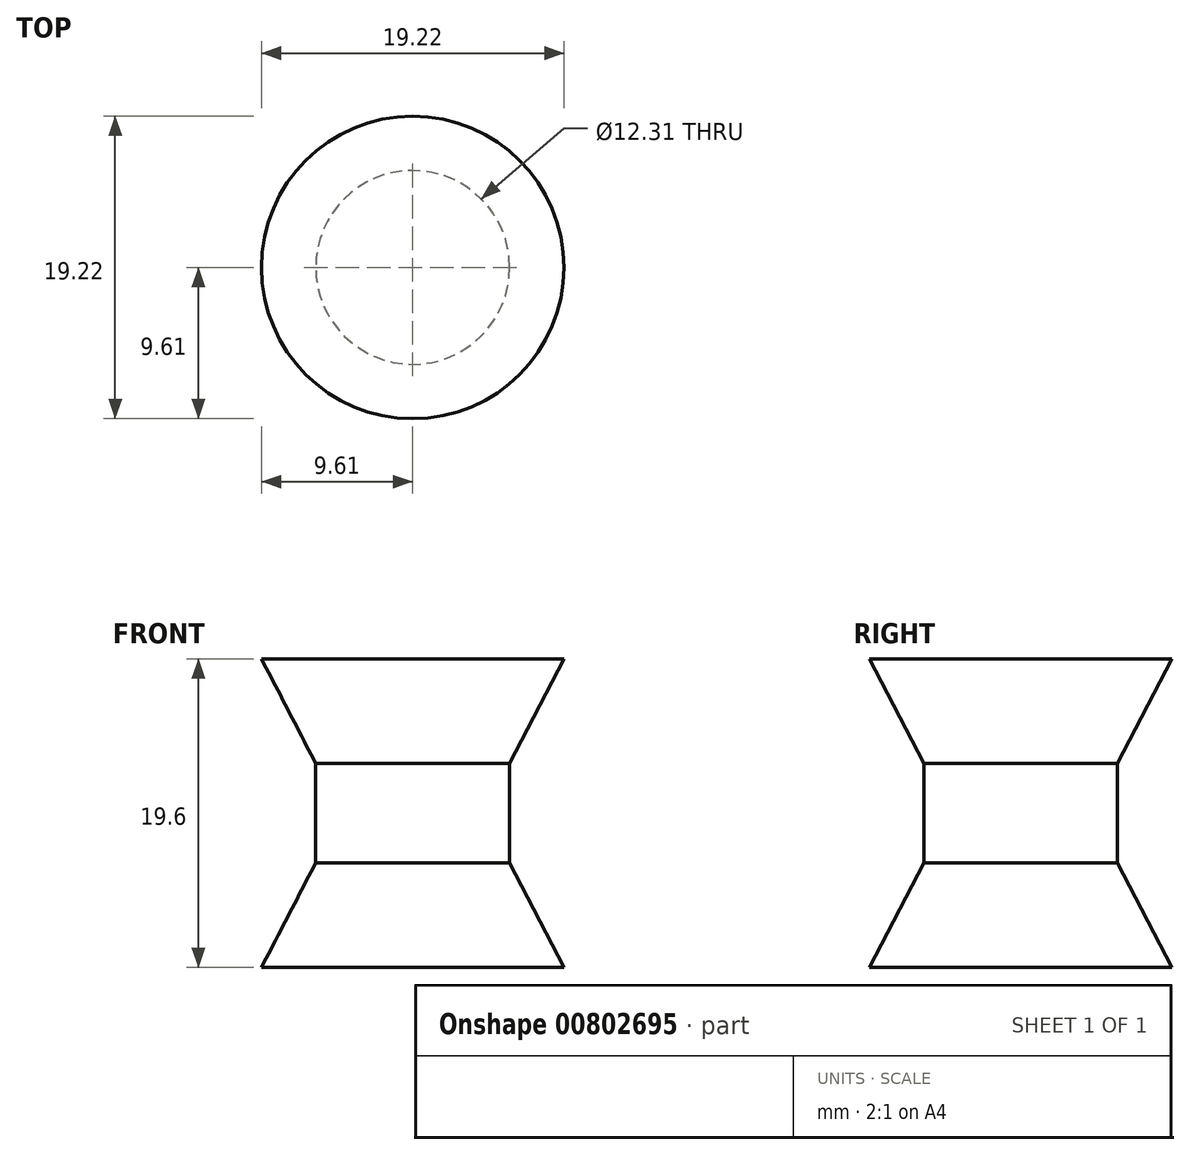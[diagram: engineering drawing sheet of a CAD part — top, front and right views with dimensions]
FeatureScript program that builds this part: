
annotation { "Feature Type Name" : "Feature", "Feature Type Description" : "" }
export const myFeature = defineFeature(function(context is Context, id is Id, definition is map)
    precondition{}
    {
        {
            var Q0;
            Q0=qCreatedBy(makeId("Front.planeOp"),FACE);
            var sketch = newSketch(context, id + "F0", { "sketchPlane" : qUnion([Q0])});
            skLineSegment(sketch, "E0", {"start": v(9.6, 9.8) * mm, "end": v(6.16, 3.15) * mm});
            skLineSegment(sketch, "E1", {"start": v(6.16, 3.15) * mm, "end": v(6.16, 0) * mm});
            skLineSegment(sketch, "E2", {"start": v(0, 0) * mm, "end": v(4.48, 0) * mm, "construction": true});
            skLineSegment(sketch, "E3.MirrorCS", {"start": v(9.6, -9.8) * mm, "end": v(6.16, -3.15) * mm});
            skLineSegment(sketch, "E4.MirrorCS", {"start": v(6.16, -3.15) * mm, "end": v(6.16, 0) * mm});
            skLineSegment(sketch, "E5", {"start": v(9.6, 9.8) * mm, "end": v(0, 9.8) * mm});
            skLineSegment(sketch, "E6", {"start": v(0, 9.8) * mm, "end": v(0, 0) * mm, "construction": true});
            skLineSegment(sketch, "E7.MirrorCS", {"start": v(9.6, -9.8) * mm, "end": v(0, -9.8) * mm});
            skSolve(sketch);
        }
        {
            var Q0;
            Q0=sQuery(id+"F0.wireOp",EDGE,"E0");
            var Q1;
            Q1=sQuery(id+"F0.wireOp",EDGE,"E1");
            var Q2;
            Q2=sQuery(id+"F0.wireOp",EDGE,"E4.MirrorCS");
            var Q3;
            Q3=sQuery(id+"F0.wireOp",EDGE,"E3.MirrorCS");
            var Q4;
            Q4=sQuery(id+"F0.wireOp",EDGE,"E5");
            var Q5;
            Q5=sQuery(id+"F0.wireOp",EDGE,"E6");
            revolve(context, id + "F1", {"bodyType" : ToolBodyType.SURFACE, "surfaceOperationType" : NewSurfaceOperationType.NEW, "surfaceEntities" : qUnion([Q0, Q1, Q2, Q3, Q4]), "axis" : qUnion([Q5]), "revolveType" : RevolveType.FULL});
        }
    });
